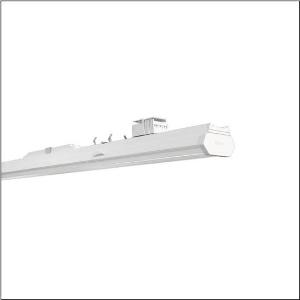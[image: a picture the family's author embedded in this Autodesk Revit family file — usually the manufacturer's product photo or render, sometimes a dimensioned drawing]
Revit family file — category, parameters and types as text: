
# Revit family: licross_r__11_protected_mo_51tp12dn495g3s4_346c
name_source: partatom
category: Lighting Fixtures
units: mm (PartAtom-declared; Revit-internal decimal feet)

## family parameters
Cut with Voids When Loaded = No
Host = Face
Light Source = No
Part Type = Normal
Room Calculation Point = No
Round Connector Dimension = Use Diameter
Shared = No

## types (1)
- --- (1 x LED, 980 lm, 6.8 W, 4000K)
    Apparent Load = 7 VA
    CIE Flux Codes = 73 92 98 99 100
    Color Rendering = 80
    Color Temperature = 4000K
    Default Elevation = 1800 mm
    Description = Licross® 11 Protected MO, luminaire insert, of sheet steel, galvanised, coil coated, white, length: 1.500mm, width: 90mm, height: 101mm, LED rated luminous flux: 9.980lm, light colour: 840, SDCM (Standard Deviation of Colour Matching)MacAdam ≤ 2 SDCM (initial), control gear: DALI 2, with plug, 6-pole, with phase selection, for trunking rail, 9 or 11-core, mains connection: 220..240V, AC, 50/60Hz, rated input power: 61W, for trunking rail, 9-/11-core, internal wiring halogen-free, for emergency light function, converter,control gear: single battery element, battery: LiFePO4, 9Ah, primary light control with lens, of plastic, primary optical cover: cover, of PMMA, light emission: direct distribution, primary light characteristic: symmetric, protection rating (complete): IP64, insulation class (complete): insulation class I (protective earthing), certification: CE, UKCA, protection symbol: D if used in an environment with conductive dust loads with corresponding accessories, impact resistance: IK06, permissible ambient temperature for indoor applications: +5..+35°C, standard: EN 60598-2-22, LABS conformity tested according to VDMA 24364:2018-05, reducing of maximum allowable ambient temperature of 5°C with ceiling mounting, corresponds to IFS (International Featured Standards) requirements for safety and quality in the food industry, packaging unit: 1 piece
    Height = 92 mm
    Lamp = 1 x LED
    Lamp Light Flux = 980 lm
    Lamp Power = 6.8 W
    Lamp count = 1
    Length = 1500 mm
    Luminous efficacy = 144 lm/W
    Manufacturer = Siteco
    ModVariant = No
    Model = 51TP12DN495G3S4
    Mounting Place = Ceiling
    Mounting Type = Pendant
    Number of Poles = 1
    OnlyDefault = Yes
    Power Factor = 1
    Product Name = Licross® 11 Protected MO
    Product group = luminaire insert | ceiling pendant
    ProductGroupID = 901
    Protection Class = Protection class I
    Protection Degree = IP 64
    RLX_Detail_Level = 1
    RLX_Emergency_Light_Flux = 0 lm
    RLX_Emergency_Type = 0
    RLX_Emergency_Type_DB = No
    RlxData = <blob elided: 24917 chars, md5=6cc4a9cb>
    Socket = socket
    Standby Power = 0 W
    System Light Flux = 980 lm
    System Power = 7 W
    Type Comments = : emergency light operation: 3 h
    Type Image = l_1256148.jpg
    URL = http://relux.com
    VarID = @adj_098351
    Voltage = 0 V
    Weight = 0.00 kg
    Width = 88 mm

## geometry (parser evidence)
native form markers: Blend x4, Sweep x10
no freeform markers — native parametric forms only
